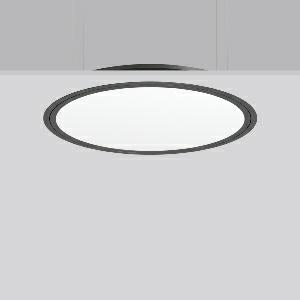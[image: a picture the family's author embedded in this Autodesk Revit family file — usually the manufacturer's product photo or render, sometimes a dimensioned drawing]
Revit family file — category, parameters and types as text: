
# Revit family: triona_round_e_312383_0031_12_d9f4
name_source: partatom
category: Lighting Fixtures
units: mm (PartAtom-declared; Revit-internal decimal feet)

## family parameters
Cut with Voids When Loaded = No
Host = Face
Light Source = No
Part Type = Normal
Room Calculation Point = No
Round Connector Dimension = Use Diameter
Shared = No

## types (1)
- TRIONA round E (1 x LED Modul 830, 6450 lm, 3000)
    Apparent Load = 70 VA
    CIE Flux Codes = 49 80 96 100 100
    Color Rendering = 80
    Color Temperature = 3000
    Default Elevation = 1800 mm
    Description = Series: TRIONA round
Decorative round LED recessed surface luminaire. Cover made of sheet steel, powder-coated. Frame made of aluminium, powder-coated. Recessed ring: aluminium extrusion profile, powder coated. Light emission through a diffuser: plastic, opal. Lightguide and diffuser made of non-yellowing plastic (PMMA). Lateral light emission (RZB SIDELITE technology) for above-average homogeneous light distribution. Suitable for installation in cavity ceilings. Tool-free mounting system thanks to the rocker arm mechanism (patent pending). Electronic ballast included. Very easy installation thanks to Plug+Play connection. 
Colour: anthracite metallic (DB703)
Diameter: 725 mm
Height: 2 mm
Cut-out diameter: 702 mm
Recess height: 100 mm
Luminaire: recess height: 89 mm
Lamp: LED
Socket: without socket
Colour temperature: 3000K
Colour rendering index (CRI): 80
System power: 70 W
Rated luminous flux: 6450 lm
Luminous efficiency: 92 lm/W
Control gear: Converter, dimmable, DALI
Protection class: I
Type of protection: IP 40
    Height = 0 mm  [stored 0 ft]
    Lamp = 1 x LED Modul 830
    Lamp Light Flux = 6450 lm
    Lamp count = 1
    Length = 725 mm
    Lifetime = 50000 h
    Luminous efficacy = 92 lm/W
    Manufacturer = RZB
    ModVariant = No
    Model = 312383.0031.12
    Mounting Place = Ceiling
    Mounting Type = Recessed
    Number of Poles = 1
    OnlyDefault = Yes
    Power Factor = 1
    Product Name = TRIONA round E
    Product group = Recessed modular luminaires
    ProductGroupID = 406
    Protection Class = Protection class I
    Protection Degree = IP 20
    RLX_Detail_Level = 1
    RLX_Emergency_Light_Flux = 0 lm
    RLX_Emergency_Type = 0
    RLX_Emergency_Type_DB = No
    RlxData = <blob elided: 39333 chars, md5=fe157f59>
    Socket = socket
    Standby Power = 0 W
    System Light Flux = 6450 lm
    System Power = 70 W
    Type Comments = Product without accessories
    Type Image = 312383.0031.12.jpg
    URL = http://relux.com
    VarID = ---
    Voltage = 230 V
    Voltage Range = 220-240 V
    Weight = 0.00 kg
    Width = 0 mm  [stored 0 ft]

note: [stored X ft] marks values corroborated as IEEE doubles in the binary element streams (Revit-internal decimal feet)

## geometry (parser evidence)
native form markers: Blend x4, Sweep x10
no freeform markers — native parametric forms only
